# Revit family: IS_Tesi_T5361_BIM_NL
name_source: partatom
category: Plumbing Fixtures
units: mm (PartAtom-declared; Revit-internal decimal feet)

## family parameters
Always vertical = No
Cut with Voids When Loaded = No
OmniClass Number = 23.45.05.21.11.11
OmniClass Title = Water Operated Water Closets
Part Type = Normal
Room Calculation Point = No
Round Connector Dimension = Use Diameter
Shared = No
Work Plane-Based = No

## types (2) — shared parameters
Afmetingen = 380 x 531 x 366 mm
AfstandsEenheid = Millimeter
Auteur = Ideal Standard
BIMobject category = Toilets
BIMobject category code = toilets
BIMobject main category = Sanitary
BIMobject main category code = sanitary
Beschrijvinggarantie = Herstellergarantie
BimObjectNaam = IS_IdealStandard_WCpans_Tesi_T5361_IdealStandard
Brand url = https://www.idealstandard.nl
Breedte = 365.9681
Date of publishing = 15/03/2023
Diepte = 531 mm
DuurEenheid = Jahre
Edition number = 1
Garantieonderdelen = https://www.idealstandard.nl
Garantieunits = Jahre
GemaaktOp = 15/03/2023
Hoogte = 379,806462510047
Hulp = https://www.idealstandard.nl
IFC Classification = Sanitary Terminal
IfcExportAs = IfcSanitaryTerminalType
IfcExportType = TOILETPAN
Installatieinstructies = https://www.idealstandard.nl
Installation instructions = https://www.idealstandard.nl
Lengte = 531 mm
Manufacturer = Ideal Standard
Manufacturer name = Ideal Standard
Masterformat 2014 Code = 10 28 13
Masterformat 2014 Description = Toilet Accessories
Materiaal = Ceramics
MateriaalWC = Ceramics
Material main = Ceramics
Merk = Ideal Standard
Montageinstuctie = https://www.idealstandard.nl
NBS Reference Code = 45-35-70/384
NBS Reference Description = WC pans
Nettogewicht = 23.83
NominalHeight = 380 mm
NominalLength = 531 mm
NominalWidth = 366 mm
OmniClass Code = 23-31 19 00
OmniClass Description = Toilets
OppervlakteEenheid = Millimeter
Product Guid = d5370db7-875b-4518-b1a1-08c4272262fe
Product SKU = T5361
Product certification = https://www.idealstandard.nl
Product data url = https://bimobject.com
Product family = TESI
Product group = Tesi
Product name = Tesi wh bowl RimLS+ incl WO seat SC BXD PB
Product url = https://www.idealstandard.nl
Productinformatie = https://www.idealstandard.nl
QR code = http://bimobject.com
Revisie = 1
Size = 380 x 531 x 366 mm
Technical description = https://www.idealstandard.nl
Telefoonnummer = 077 355 08 08
Toepassing = WC Pans
TypeWC = Wand aufgehängt
Typeconnectie = Installation
TypespoelingWC = afspoelen
UNSPSC Code = 301815
URL = https://www.idealstandard.nl
Uniclass 2015 Code = Pr_40_20_93_94
Uniclass 2015 Name = WC pans
Uniclass2015Beschrijving = WC pans
Uniclass2015Referentie = Pr_40_20_93_94
Uniclass2015Version = v1.26
Uniformat II Code = D2010
Uniformat II Description = Plumbing Fixtures
Urlproducent = https://www.idealstandard.nl
ValutaEenheid = Euro
Versie = 1
Verwachtelevensduur = 99
Volumeunits = Liter
Vorm = geformt
Wisselstukken = https://www.idealstandard.nl
Youtube clip = https://www.youtube.com
zero-valued in all types: BrutoGewicht, Cost, Default Elevation, Vervangingskosten

## per-type parameters (varying)
| type | Afwerking | Artikelnummer | Artikelomschrijving | Artikelreferentie | Barcode | Description | Eigenschappen | GTIN code | Kleur | Kleurwc | Model | Referentie |
| T536101 - Tesi wall mounted bowl RimLS+ EASY FIX+ and SOFT CLOSE Seat & Cover Wrapover in PICTURE carton box, in white | Weiß | T536101 | Ideal Standard Tesi Wandtiefspül-WC RimLS+ EASY FIX+ und SOFT CLOSE Sitz & Deckel Wrapover in ABGEBILDETEN Kartonverpackung, in Weiß | T536101 | 8014140509646 | Tesi Wandtiefspül-WC RimLS+ EASY FIX+ und SOFT CLOSE Sitz & Deckel Wrapover in ABGEBILDETEN Kartonverpackung, in Weiß | Wandtiefspül-WC RimLS+ EASY FIX+ und SOFT CLOSE Sitz & Deckel Wrapover in ABGEBILDETEN Kartonverpackung, in Weiß | 8014140509646 | Weiß | Weiß | T536101 | Ideal Standard Tesi Wandtiefspül-WC RimLS+ EASY FIX+ und SOFT CLOSE Sitz & Deckel Wrapover in ABGEBILDETEN Kartonverpackung, in Weiß |
| T5361V3 - Tesi wall mounted bowl RimLS+ EASY FIX+ and SOFT CLOSE Seat & Cover Wrapover in PICTURE carton box, in SILK BLACK | Seidenschwarz | T5361V3 | Ideal Standard Tesi Wandtiefspül-WC RimLS+ EASY FIX+ und SOFT CLOSE Sitz & Deckel Wrapover in ABGEBILDETEN Kartonverpackung, in Seidenschwarz | T5361V3 | 8014140511489 | Tesi Wandtiefspül-WC RimLS+ EASY FIX+ und SOFT CLOSE Sitz & Deckel Wrapover in ABGEBILDETEN Kartonverpackung, in Seidenschwarz | Wandtiefspül-WC RimLS+ EASY FIX+ und SOFT CLOSE Sitz & Deckel Wrapover in ABGEBILDETEN Kartonverpackung, in Seidenschwarz | 8014140511489 | Seidenschwarz | Seidenschwarz | T5361V3 | Ideal Standard Tesi Wandtiefspül-WC RimLS+ EASY FIX+ und SOFT CLOSE Sitz & Deckel Wrapover in ABGEBILDETEN Kartonverpackung, in Seidenschwarz |

## geometry (parser evidence)
native form markers: Blend x4, Sweep x2
no freeform markers — native parametric forms only
